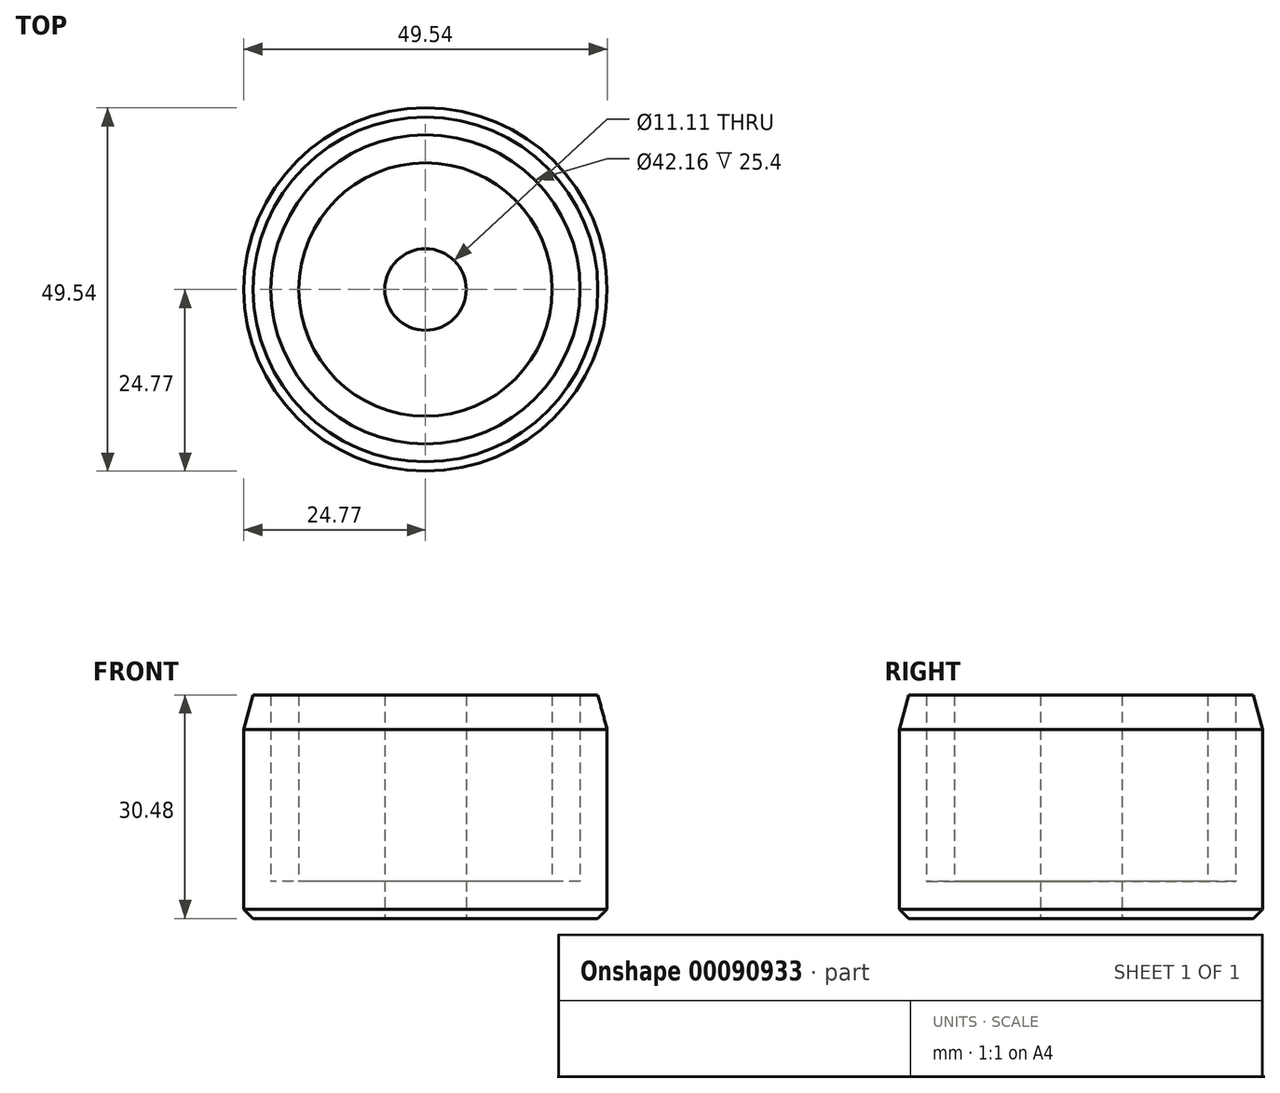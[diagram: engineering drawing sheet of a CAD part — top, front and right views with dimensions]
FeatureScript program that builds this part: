
annotation { "Feature Type Name" : "Feature", "Feature Type Description" : "" }
export const myFeature = defineFeature(function(context is Context, id is Id, definition is map)
    precondition{}
    {
        {
            var Q0;
            Q0=qCreatedBy(makeId("Top.planeOp"),FACE);
            var sketch = newSketch(context, id + "F0", { "sketchPlane" : qUnion([Q0])});
            skCircle(sketch, "E0", {"center": v(0, 0) * mm, "radius": 5.56 * mm});
            skCircle(sketch, "E1", {"center": v(0, 0) * mm, "radius": 17.27 * mm});
            skCircle(sketch, "E2", {"center": v(0, 0) * mm, "radius": 21.08 * mm});
            skCircle(sketch, "E3", {"center": v(0, 0) * mm, "radius": 24.77 * mm});
            skSolve(sketch);
        }
        {
            var Q0;
            Q0 = qSketchRegion(id + "F0", true);
            var Q1;
            Q1=makeQuery(id+"F0.imprint","IMPRINT",FACE,{"disambiguationData":[TD([[makeQuery(id+"F0.imprint","IMPRINT",EDGE,{"derivedFrom":sQuery(id+"F0.wireOp",EDGE,"E0")}),-1.0]])]});
            extrude(context, id + "F1", {"entities" : qUnion([Q0, Q1]), "depth" : 30.48 * mm});
        }
        {
            var Q0;
            Q0=makeQuery(id+"F0.imprint","IMPRINT",FACE,{"disambiguationData":[TD([[makeQuery(id+"F0.imprint","IMPRINT",EDGE,{"derivedFrom":sQuery(id+"F0.wireOp",EDGE,"E1")}),-1.0]])]});
            extrude(context, id + "F2", {"entities" : qUnion([Q0]), "operationType" : NewBodyOperationType.ADD, "depth" : 5.08 * mm});
        }
        {
            var Q0;
            Q0=makeQuery(id+"F1.opExtrude","CAP_EDGE",EDGE,{"disambiguationData":[OSD([sQuery(id+"F0.wireOp",EDGE,"E3")])],"isStart":false});
            chamfer(context, id + "F3", {"entities" : qUnion([Q0]), "chamferType" : ChamferType.OFFSET_ANGLE, "width" : 1.27 * mm, "oppositeDirection" : false, "angle" : 75 * degree, "tangentPropagation" : true});
        }
        {
            var Q0;
            Q0=makeQuery(id+"F1.opExtrude","CAP_EDGE",EDGE,{"disambiguationData":[OSD([sQuery(id+"F0.wireOp",EDGE,"E3")])],"isStart":true});
            chamfer(context, id + "F4", {"entities" : qUnion([Q0]), "width" : 1.27 * mm, "tangentPropagation" : true});
        }
    });
